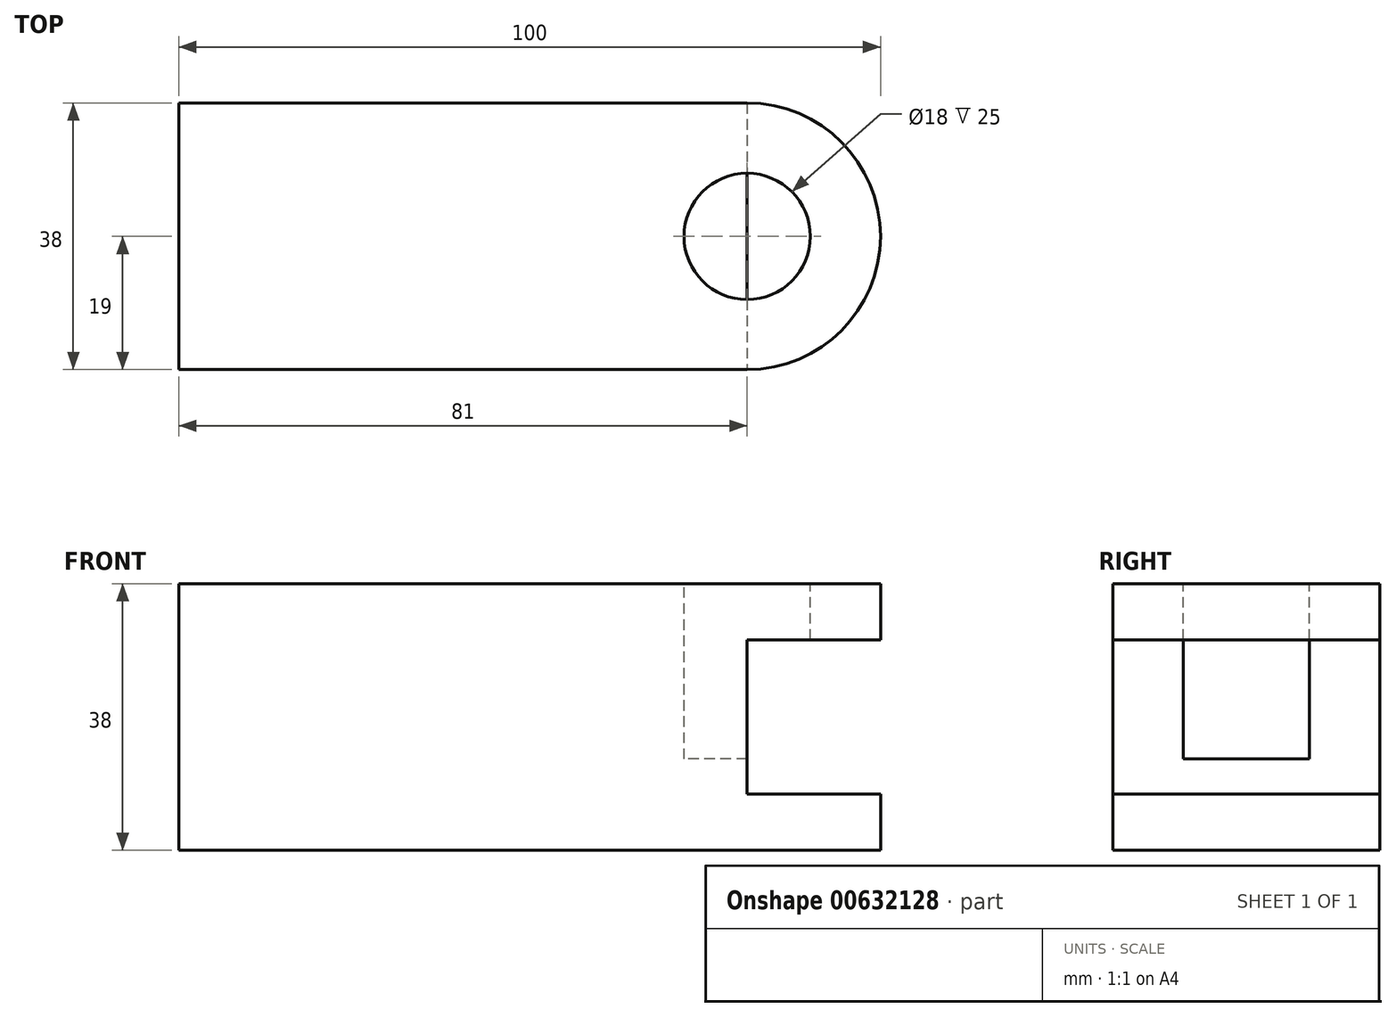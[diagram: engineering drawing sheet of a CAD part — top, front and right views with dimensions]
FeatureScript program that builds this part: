
annotation { "Feature Type Name" : "Feature", "Feature Type Description" : "" }
export const myFeature = defineFeature(function(context is Context, id is Id, definition is map)
    precondition{}
    {
        {
            var Q0;
            Q0=qCreatedBy(makeId("Top.planeOp"),FACE);
            var sketch = newSketch(context, id + "F0", { "sketchPlane" : qUnion([Q0])});
            skLineSegment(sketch, "E0.bottom", {"start": v(0, 0) * mm, "end": v(100, 0) * mm});
            skLineSegment(sketch, "E0.top", {"start": v(0, 38) * mm, "end": v(100, 38) * mm});
            skLineSegment(sketch, "E0.left", {"start": v(0, 0) * mm, "end": v(0, 38) * mm});
            skLineSegment(sketch, "E0.right", {"start": v(100, 0) * mm, "end": v(100, 38) * mm});
            skSolve(sketch);
        }
        {
            var Q0;
            Q0=makeQuery(id+"F0.imprint","IMPRINT",FACE,{"disambiguationData":[TD([[makeQuery(id+"F0.imprint","IMPRINT",EDGE,{"derivedFrom":sQuery(id+"F0.wireOp",EDGE,"E0.bottom")}),1.0]])]});
            extrude(context, id + "F1", {"entities" : qUnion([Q0]), "depth" : 38 * mm, "offsetDistance" : 25 * mm});
        }
        {
            var Q0;
            Q0=makeQuery(id+"F1.opExtrude","SWEPT_EDGE",EDGE,{"disambiguationData":[OSD([sQuery(id+"F0.wireOp",EDGE,"E0.bottom"),sQuery(id+"F0.wireOp",EDGE,"E0.right")])]});
            var Q1;
            Q1=makeQuery(id+"F1.opExtrude","SWEPT_EDGE",EDGE,{"disambiguationData":[OSD([sQuery(id+"F0.wireOp",EDGE,"E0.top"),sQuery(id+"F0.wireOp",EDGE,"E0.right")])]});
            fillet(context, id + "F2", {"entities" : qUnion([Q0, Q1]), "radius" : 19 * mm, "tangentPropagation" : true, "allowEdgeOverflow" : false});
        }
        {
            var Q0;
            Q0=makeQuery(id+"F1.opExtrude","CAP_FACE",FACE,{"disambiguationData":[OSD([sQuery(id+"F0.wireOp",EDGE,"E0.bottom"),sQuery(id+"F0.wireOp",EDGE,"E0.top"),sQuery(id+"F0.wireOp",EDGE,"E0.left"),sQuery(id+"F0.wireOp",EDGE,"E0.right")])],"isStart":false});
            var sketch = newSketch(context, id + "F3", { "sketchPlane" : qUnion([Q0])});
            skCircle(sketch, "E1", {"center": v(81, 19) * mm, "radius": 9 * mm});
            skSolve(sketch);
        }
        {
            var Q0;
            Q0=makeQuery(id+"F3.imprint","IMPRINT",FACE,{"disambiguationData":[TD([[makeQuery(id+"F3.imprint","IMPRINT",EDGE,{"derivedFrom":sQuery(id+"F3.wireOp",EDGE,"E1")}),1.0]])]});
            extrude(context, id + "F4", {"entities" : qUnion([Q0]), "operationType" : NewBodyOperationType.REMOVE, "oppositeDirection" : true, "depth" : 25 * mm, "offsetDistance" : 25 * mm});
        }
        {
            var Q0;
            Q0=makeQuery(id+"F1.opExtrude","SWEPT_FACE",FACE,{"disambiguationData":[OSD([sQuery(id+"F0.wireOp",EDGE,"E0.bottom")])]});
            var sketch = newSketch(context, id + "F5", { "sketchPlane" : qUnion([Q0])});
            skLineSegment(sketch, "E2.bottom", {"start": v(71.92, 30) * mm, "end": v(101.32, 30) * mm});
            skLineSegment(sketch, "E2.top", {"start": v(71.92, 8) * mm, "end": v(101.32, 8) * mm});
            skLineSegment(sketch, "E2.left", {"start": v(71.92, 30) * mm, "end": v(71.92, 8) * mm});
            skLineSegment(sketch, "E2.right", {"start": v(101.32, 30) * mm, "end": v(101.32, 8) * mm});
            skSolve(sketch);
        }
        {
            var Q0;
            {var subQ0=sQuery(id+"F5.wireOp",EDGE,"E2.right");Q0=makeQuery(id+"F5.imprint","IMPRINT",FACE,{"disambiguationData":[TD([[makeQuery(id+"F5.imprint","IMPRINT",EDGE,{"derivedFrom":subQ0}),-1.0]])]});}
            extrude(context, id + "F6", {"entities" : qUnion([Q0]), "operationType" : NewBodyOperationType.REMOVE, "endBound" : BoundingType.THROUGH_ALL, "oppositeDirection" : true, "depth" : 25 * mm, "offsetDistance" : 25 * mm});
        }
    });
